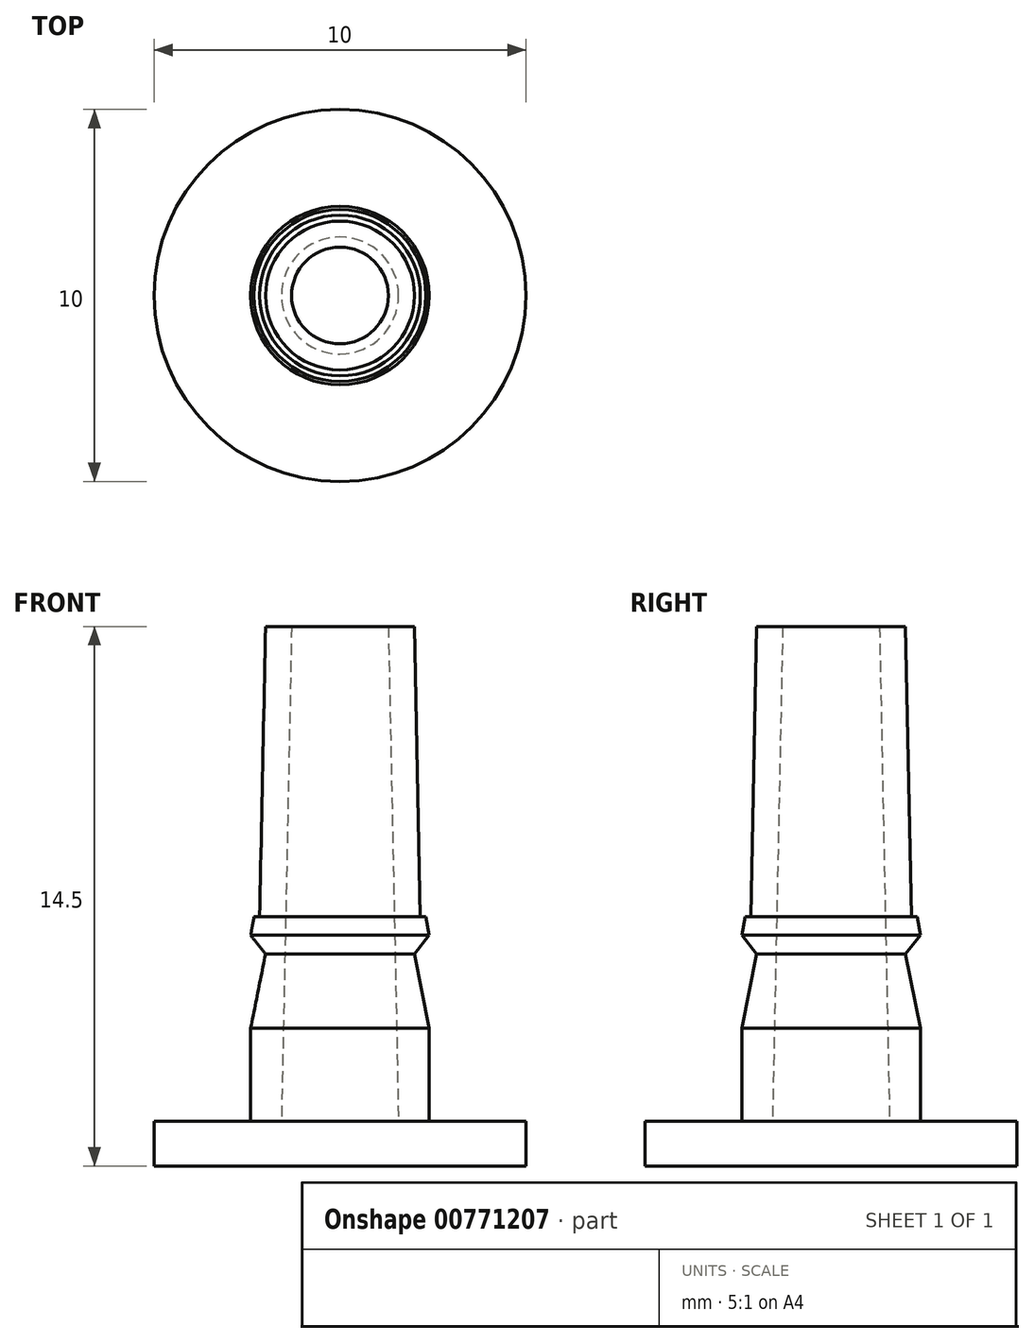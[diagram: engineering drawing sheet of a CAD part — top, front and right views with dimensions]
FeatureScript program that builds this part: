
annotation { "Feature Type Name" : "Feature", "Feature Type Description" : "" }
export const myFeature = defineFeature(function(context is Context, id is Id, definition is map)
    precondition{}
    {
        {
            var Q0;
            Q0=qCreatedBy(makeId("Front.planeOp"),FACE);
            var sketch = newSketch(context, id + "F0", { "sketchPlane" : qUnion([Q0])});
            skLineSegment(sketch, "E0", {"start": v(0, 0) * mm, "end": v(5, 0) * mm});
            skLineSegment(sketch, "E1", {"start": v(0, 0) * mm, "end": v(0, 14.5) * mm});
            skLineSegment(sketch, "E2", {"start": v(5, 0) * mm, "end": v(5, 1.2) * mm});
            skLineSegment(sketch, "E3", {"start": v(2.4, 1.2) * mm, "end": v(2.4, 3.7) * mm});
            skLineSegment(sketch, "E4", {"start": v(2, 5.7) * mm, "end": v(2.4, 3.7) * mm});
            skLineSegment(sketch, "E5", {"start": v(2.4, 6.2) * mm, "end": v(2.31, 6.7) * mm});
            skLineSegment(sketch, "E6", {"start": v(0, 14.5) * mm, "end": v(2, 14.5) * mm});
            skLineSegment(sketch, "E7", {"start": v(2, 14.5) * mm, "end": v(2.16, 6.7) * mm});
            skLineSegment(sketch, "E8", {"start": v(2.31, 6.7) * mm, "end": v(2.16, 6.7) * mm});
            skLineSegment(sketch, "E9", {"start": v(2.4, 1.2) * mm, "end": v(5, 1.2) * mm});
            skLineSegment(sketch, "E10", {"start": v(2.4, 1.2) * mm, "end": v(0, 1.2) * mm});
            skPoint(sketch, "E11", {"position": v(1.3, 14.5) * mm});
            skLineSegment(sketch, "E12", {"start": v(1.3, 14.5) * mm, "end": v(1.57, 1.2) * mm});
            skLineSegment(sketch, "E13", {"start": v(2.4, 6.2) * mm, "end": v(2, 5.7) * mm});
            skSolve(sketch);
        }
        {
            var Q0;
            {var subQ1=sQuery(id+"F0.wireOp",EDGE,"E3");Q0=makeQuery(id+"F0.imprint","IMPRINT",FACE,{"disambiguationData":[TD([[makeQuery(id+"F0.imprint","IMPRINT",EDGE,{"derivedFrom":subQ1}),1.0]])]});}
            var Q1;
            {var subQ4=sQuery(id+"F0.wireOp",EDGE,"E0");Q1=makeQuery(id+"F0.imprint","IMPRINT",FACE,{"disambiguationData":[TD([[makeQuery(id+"F0.imprint","IMPRINT",EDGE,{"derivedFrom":subQ4}),1.0]])]});}
            var Q2;
            Q2=sQuery(id+"F0.wireOp",EDGE,"E1");
            revolve(context, id + "F1", {"surfaceOperationType" : NewSurfaceOperationType.NEW, "entities" : qUnion([Q0, Q1]), "axis" : qUnion([Q2]), "revolveType" : RevolveType.FULL});
        }
    });
